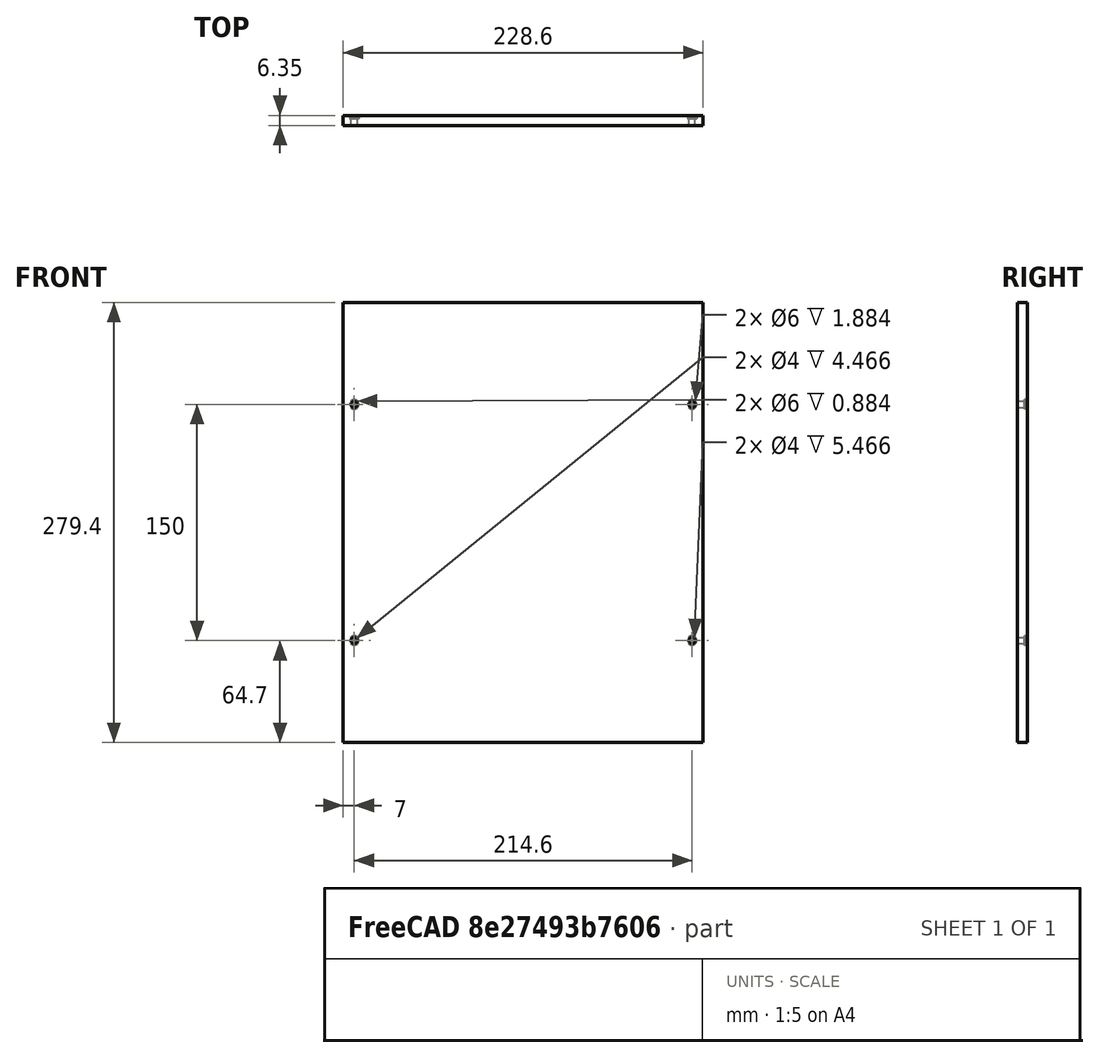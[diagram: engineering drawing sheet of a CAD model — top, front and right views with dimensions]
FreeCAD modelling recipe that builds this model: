
FCSTD DOCUMENT  (FreeCAD 0.17R10423 (Git))
Label: bed_plate
License: All rights reserved
LicenseURL: http://en.wikipedia.org/wiki/All_rights_reserved
objects: Part::Box×2, Part::Feature×1, App::FeaturePython×1, Part::MultiFuse×1
note: 4 computed .brp shape members not serialized (recipe doc carries the construction recipe); baked Part::Feature solids carry a one-line shape summary decoded from their .brp

FEATURE [Part::Feature] Part__Feature095  label="Bed Plate"
  Placement = pos=(150.2,98.2,260) rot=(0,0,1;0rad)
  shape: bbox 228.6 x 6.35 x 228.6 mm, 18 faces (baked)
FEATURE [Part::Box] Box  label="Cube"
  AttacherType = Attacher::AttachEngine3D
  Height = 25.4
  Length = 228.6
  Placement = pos=(35.9,98.2,374.3) rot=(0,0,1;0rad)
  Width = 6.35
FEATURE [Part::Box] Box001  label="Cube001"
  AttacherType = Attacher::AttachEngine3D
  Height = 25.4
  Length = 228.6
  Placement = pos=(35.9,98.2,120.3) rot=(0,0,1;0rad)
  Width = 6.35
FEATURE [App::FeaturePython] planeConstraint01  # a2plus constraint (typed FeaturePython)
  Object1 = Box
  Object2 = Part__Feature095
  SubElement1 = Face4
  SubElement2 = Face17
  Type = plane
  directionConstraint = 0
  offset = 0
FEATURE [Part::MultiFuse] Fusion
  Shapes = -> [Part__Feature095,Box,Box001]
